# Revit family: DBLTD_TheSenatorGroup_OfficeChairs_Curve
name_source: partatom
category: Furniture
units: mm (PartAtom-declared; Revit-internal decimal feet)

## family parameters
Always vertical = Yes
Cut with Voids When Loaded = No
OmniClass Number = 23.40.20.00
OmniClass Title = General Furniture and Specialties
Render Appearance Source = Family Geometry
Room Calculation Point = No
Shared = Yes
Work Plane-Based = No

## types (2) — shared parameters
Assembly Code = E2020200
AssetType = Movable
Category = Pr_40_50_12_57 Office chairs
Color = Seat, Back and Frame: Solid Oak
Constituents = Seat, Back and Frame
DurationUnit = years
ExpectedLife = 5
Finish = Seat, Back and Frame: Solid Oak
Keynote = Pr_40_50_12_57 Office chairs
Manufacturer = The Senator Group
ManufacturerName = The Senator Group
ManufacturerURL = https://www.allermuir.com
Material = Seat, Back and Frame: Solid Oak
Name = Chair
NominalDepth = 650 mm  [stored 2.13255 ft]
NominalHeight = 735 mm
NominalWidth = 830 mm  [stored 2.7231 ft]
ProductInformation = https://www.allermuir.com
SeatingHeight = 406 mm
Shape = Rectangular
Size = 735 h x 830 w x 650 d mm
URL = https://www.thesenatorgroup.com
Uniclass2015Code = Pr_40_50_12_57
Uniclass2015Title = Office chairs
Uniclass2015Version = Products v1.15
Version = 1
WarrantyDescription = The Senator Group warrants that its manufactured products are free from manufacturing defects - in materials or workmanship - for a period of five (5) years.
WarrantyDurationLabor = 5
WarrantyDurationParts = 5
WarrantyDurationUnit = years
WarrantyGuarantorLabor = https://www.allermuir.com
WarrantyGuarantorParts = https://www.allermuir.com
zero-valued in all types: Cost, Default Elevation

## per-type parameters (varying)
| type | HasSolidOakSeat | HasUpholsteredSeatPad | Model | ModelNumber |
| Lounge Chair | Yes | No | CUR101 | CUR101 |
| Lounge Chair with Upholstered Seat Pad | No | Yes | CUR101U1 | CUR101U1 |

note: column(s) folded — value = type name in every type: Description, ModelReference, Type Comments

note: [stored X ft] marks values corroborated as IEEE doubles in the binary element streams (Revit-internal decimal feet)

## geometry (parser evidence)
native form markers: Sweep x2
no freeform markers — native parametric forms only
